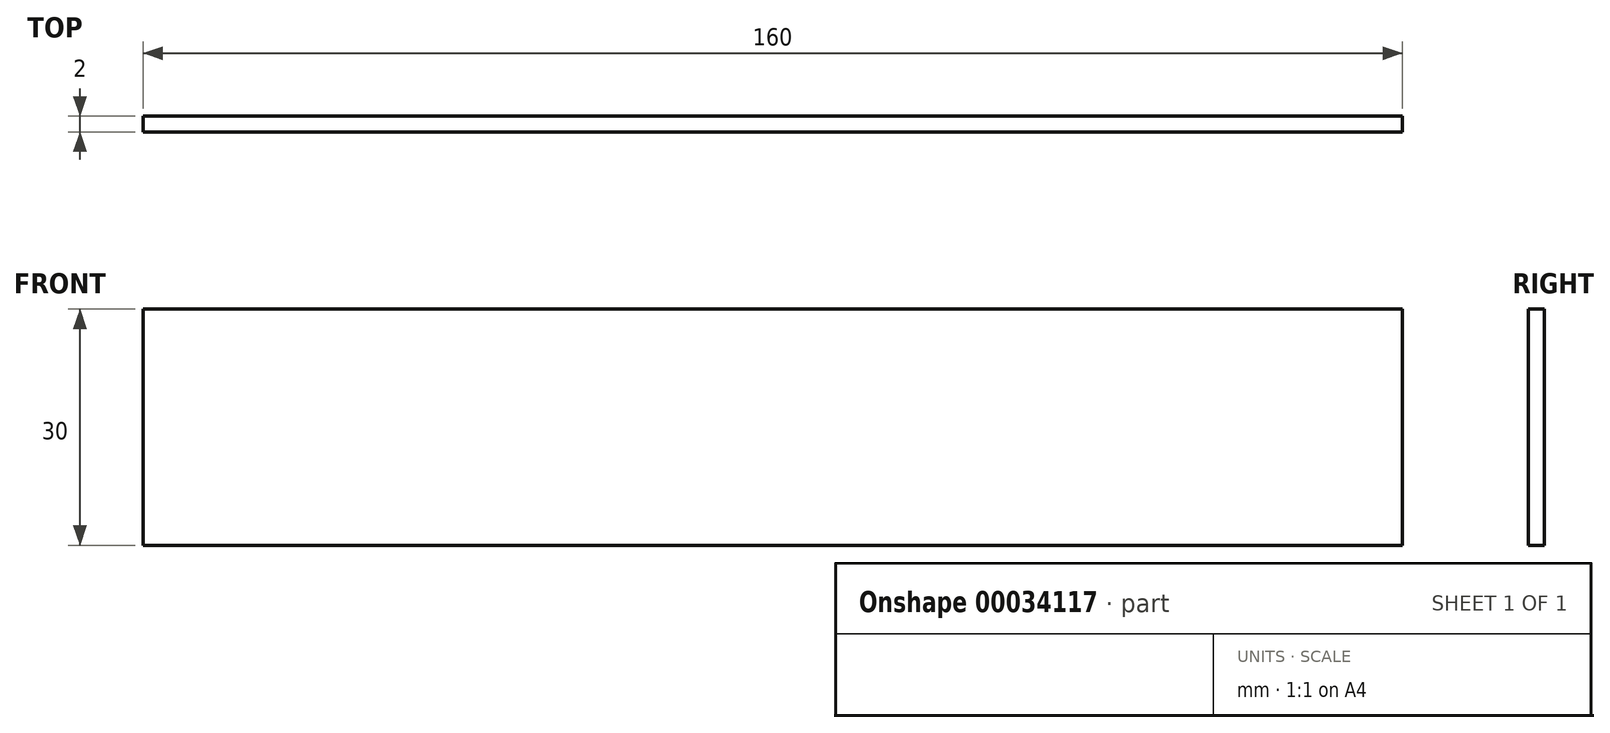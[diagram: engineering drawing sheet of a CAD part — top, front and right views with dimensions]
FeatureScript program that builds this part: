
annotation { "Feature Type Name" : "Feature", "Feature Type Description" : "" }
export const myFeature = defineFeature(function(context is Context, id is Id, definition is map)
    precondition{}
    {
        {
            var Q0;
            Q0=qCreatedBy(makeId("Front.planeOp"),FACE);
            var sketch = newSketch(context, id + "F0", { "sketchPlane" : qUnion([Q0])});
            skPoint(sketch, "E0.rect.middle", {"position": v(0, 0) * mm});
            skLineSegment(sketch, "E1.rect.bottom", {"start": v(80, -15) * mm, "end": v(-80, -15) * mm});
            skLineSegment(sketch, "E1.rect.top", {"start": v(80, 15) * mm, "end": v(-80, 15) * mm});
            skLineSegment(sketch, "E1.rect.left", {"start": v(80, -15) * mm, "end": v(80, 15) * mm});
            skLineSegment(sketch, "E1.rect.right", {"start": v(-80, -15) * mm, "end": v(-80, 15) * mm});
            skSolve(sketch);
        }
        {
            var Q0;
            Q0=qSketchRegion(id+"F0",true);
            extrude(context, id + "F1", {"entities" : qUnion([Q0]), "depth" : 2 * mm});
        }
    });
